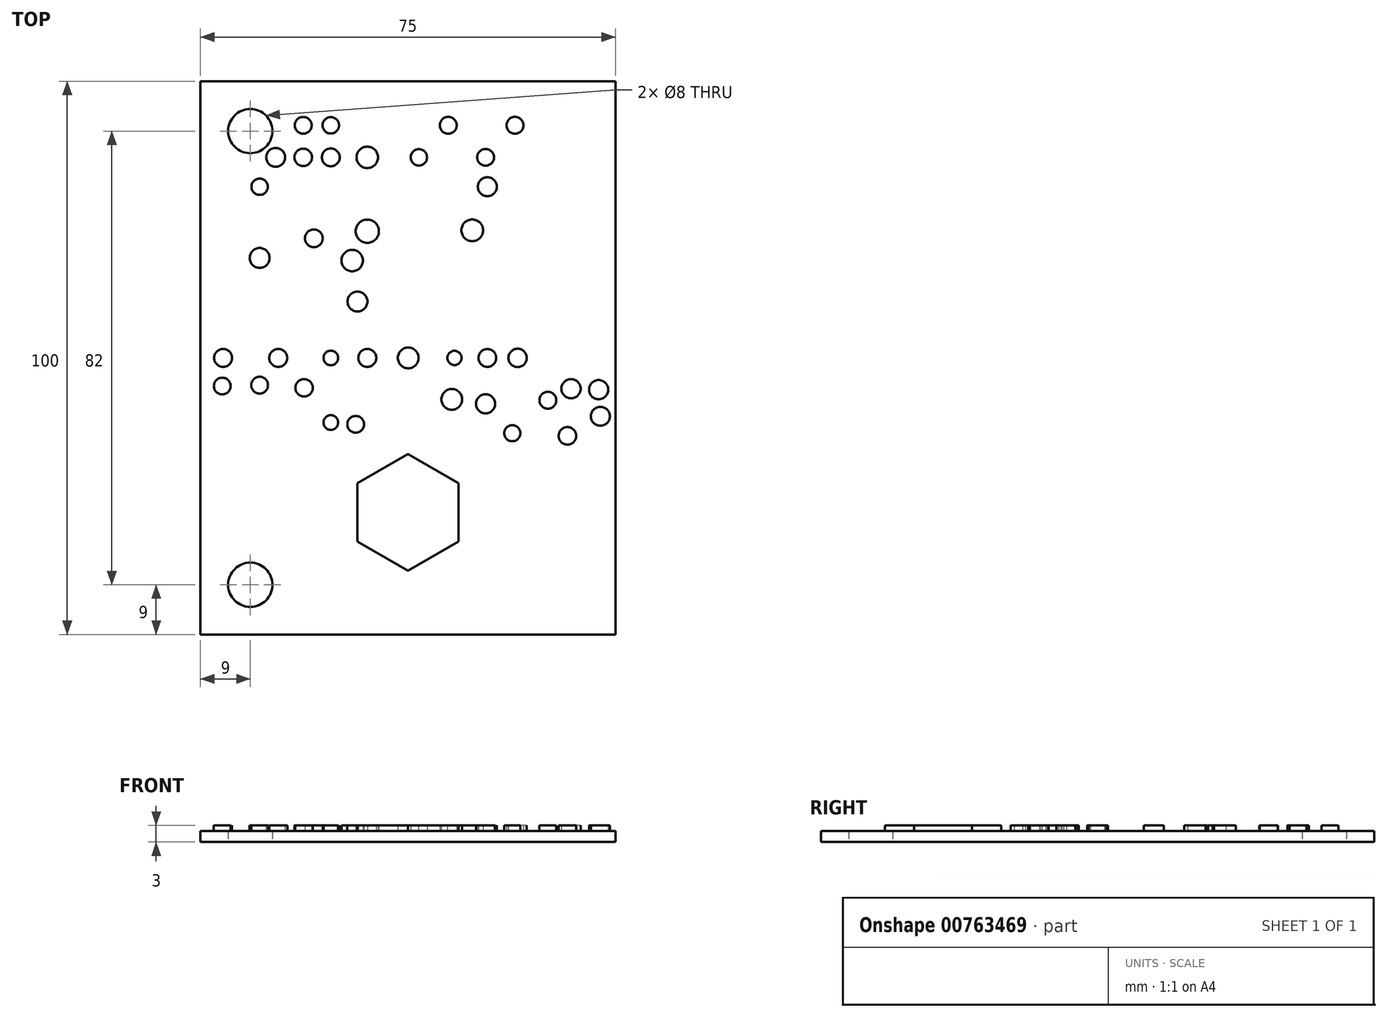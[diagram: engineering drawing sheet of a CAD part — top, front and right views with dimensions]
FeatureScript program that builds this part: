
annotation { "Feature Type Name" : "Feature", "Feature Type Description" : "" }
export const myFeature = defineFeature(function(context is Context, id is Id, definition is map)
    precondition{}
    {
        {
            var Q0;
            Q0=qCreatedBy(makeId("Top.planeOp"),FACE);
            var sketch = newSketch(context, id + "F0", { "sketchPlane" : qUnion([Q0])});
            skLineSegment(sketch, "E0.bottom", {"start": v(-37.5, 50) * mm, "end": v(37.5, 50) * mm});
            skLineSegment(sketch, "E0.top", {"start": v(-37.5, -50) * mm, "end": v(37.5, -50) * mm});
            skLineSegment(sketch, "E0.left", {"start": v(-37.5, 50) * mm, "end": v(-37.5, -50) * mm});
            skLineSegment(sketch, "E0.right", {"start": v(37.5, 50) * mm, "end": v(37.5, -50) * mm});
            skPoint(sketch, "E0.middle", {"position": v(0, 0) * mm});
            skCircle(sketch, "E1", {"center": v(-28.5, 41) * mm, "radius": 4 * mm});
            skCircle(sketch, "E2", {"center": v(-28.5, -41) * mm, "radius": 4 * mm});
            skSolve(sketch);
        }
        {
            var Q0;
            Q0 = qSketchRegion(id + "F0", true);
            var Q1;
            Q1=makeQuery(id+"F0.imprint","IMPRINT",FACE,{"disambiguationData":[TD([[makeQuery(id+"F0.imprint","IMPRINT",EDGE,{"derivedFrom":sQuery(id+"F0.wireOp",EDGE,"E0.bottom")}),-1.0]])]});
            extrude(context, id + "F1", {"entities" : qUnion([Q0, Q1]), "depth" : 2 * mm, "offsetDistance" : 25 * mm});
        }
        {
            var Q0;
            Q0=makeQuery(id+"F1.opExtrude","CAP_FACE",FACE,{"disambiguationData":[OSD([sQuery(id+"F0.wireOp",EDGE,"E0.bottom"),sQuery(id+"F0.wireOp",EDGE,"E0.top"),sQuery(id+"F0.wireOp",EDGE,"E0.left"),sQuery(id+"F0.wireOp",EDGE,"E0.right"),sQuery(id+"F0.wireOp",EDGE,"E1"),sQuery(id+"F0.wireOp",EDGE,"E2")])],"isStart":false});
            var sketch = newSketch(context, id + "F2", { "sketchPlane" : qUnion([Q0])});
            skCircle(sketch, "E3", {"center": v(-18.93, 42.04) * mm, "radius": 1.52 * mm});
            skCircle(sketch, "E4", {"center": v(-18.93, 36.25) * mm, "radius": 1.58 * mm});
            skCircle(sketch, "E5", {"center": v(-23.92, 36.25) * mm, "radius": 1.7 * mm});
            skCircle(sketch, "E6", {"center": v(-26.81, 30.95) * mm, "radius": 1.48 * mm});
            skCircle(sketch, "E7", {"center": v(-13.95, 36.25) * mm, "radius": 1.6 * mm});
            skCircle(sketch, "E8", {"center": v(-7.35, 36.25) * mm, "radius": 1.94 * mm});
            skCircle(sketch, "E9", {"center": v(-13.95, 42.04) * mm, "radius": 1.48 * mm});
            skCircle(sketch, "E10", {"center": v(1.98, 36.25) * mm, "radius": 1.48 * mm});
            skCircle(sketch, "E11", {"center": v(7.28, 42.04) * mm, "radius": 1.53 * mm});
            skCircle(sketch, "E12", {"center": v(14.36, 30.95) * mm, "radius": 1.7 * mm});
            skCircle(sketch, "E13", {"center": v(14.04, 36.25) * mm, "radius": 1.52 * mm});
            skCircle(sketch, "E14", {"center": v(19.35, 42.04) * mm, "radius": 1.53 * mm});
            skCircle(sketch, "E15", {"center": v(-26.81, 18.08) * mm, "radius": 1.8 * mm});
            skCircle(sketch, "E16", {"center": v(-17, 21.62) * mm, "radius": 1.6 * mm});
            skCircle(sketch, "E17", {"center": v(-9.12, 10.2) * mm, "radius": 1.8 * mm});
            skCircle(sketch, "E18", {"center": v(-10.09, 17.6) * mm, "radius": 1.94 * mm});
            skCircle(sketch, "E19", {"center": v(-7.35, 22.9) * mm, "radius": 2.1 * mm});
            skCircle(sketch, "E20", {"center": v(11.63, 23.07) * mm, "radius": 1.96 * mm});
            skCircle(sketch, "E21", {"center": v(-33.4, 0) * mm, "radius": 1.63 * mm});
            skCircle(sketch, "E22", {"center": v(-33.57, -5.08) * mm, "radius": 1.52 * mm});
            skCircle(sketch, "E23", {"center": v(-26.81, -4.92) * mm, "radius": 1.52 * mm});
            skCircle(sketch, "E24", {"center": v(-18.77, -5.4) * mm, "radius": 1.58 * mm});
            skCircle(sketch, "E25", {"center": v(-23.44, 0) * mm, "radius": 1.63 * mm});
            skCircle(sketch, "E26", {"center": v(-13.95, -11.68) * mm, "radius": 1.33 * mm});
            skCircle(sketch, "E27", {"center": v(-9.44, -12) * mm, "radius": 1.52 * mm});
            skCircle(sketch, "E28", {"center": v(-13.95, 0) * mm, "radius": 1.32 * mm});
            skCircle(sketch, "E29", {"center": v(-7.35, 0) * mm, "radius": 1.62 * mm});
            skCircle(sketch, "E30", {"center": v(0.05, 0) * mm, "radius": 1.87 * mm});
            skCircle(sketch, "E31", {"center": v(7.93, -7.5) * mm, "radius": 1.88 * mm});
            skCircle(sketch, "E32", {"center": v(14.04, -8.3) * mm, "radius": 1.73 * mm});
            skCircle(sketch, "E33", {"center": v(8.41, 0) * mm, "radius": 1.3 * mm});
            skCircle(sketch, "E34", {"center": v(14.36, 0) * mm, "radius": 1.6 * mm});
            skCircle(sketch, "E35", {"center": v(18.86, -13.6) * mm, "radius": 1.46 * mm});
            skCircle(sketch, "E36", {"center": v(25.3, -7.65) * mm, "radius": 1.53 * mm});
            skCircle(sketch, "E37", {"center": v(19.83, 0) * mm, "radius": 1.66 * mm});
            skCircle(sketch, "E38", {"center": v(28.84, -14.09) * mm, "radius": 1.58 * mm});
            skCircle(sketch, "E39", {"center": v(34.79, -10.55) * mm, "radius": 1.7 * mm});
            skCircle(sketch, "E40", {"center": v(34.47, -5.72) * mm, "radius": 1.73 * mm});
            skCircle(sketch, "E41", {"center": v(29.48, -5.56) * mm, "radius": 1.74 * mm});
            skCircle(sketch, "E42.cCircle", {"center": v(0, -27.92) * mm, "radius": 9.12 * mm, "construction": true});
            skLineSegment(sketch, "E42.0", {"start": v(-9.12, -33.19) * mm, "end": v(-9.12, -22.65) * mm});
            skLineSegment(sketch, "E42.1", {"start": v(-9.12, -22.65) * mm, "end": v(0, -17.39) * mm});
            skLineSegment(sketch, "E42.2", {"start": v(0, -17.39) * mm, "end": v(9.12, -22.65) * mm});
            skLineSegment(sketch, "E42.3", {"start": v(9.12, -22.65) * mm, "end": v(9.12, -33.19) * mm});
            skLineSegment(sketch, "E42.4", {"start": v(9.12, -33.19) * mm, "end": v(0, -38.45) * mm});
            skLineSegment(sketch, "E42.5", {"start": v(0, -38.45) * mm, "end": v(-9.12, -33.19) * mm});
            skPoint(sketch, "E42.0.midPoint", {"position": v(-9.12, -27.92) * mm});
            skSolve(sketch);
        }
        {
            var Q0;
            Q0=makeQuery(id+"F2.imprint","IMPRINT",FACE,{"disambiguationData":[TD([[makeQuery(id+"F2.imprint","IMPRINT",EDGE,{"derivedFrom":sQuery(id+"F2.wireOp",EDGE,"E42.0")}),-1.0]])]});
            var Q1;
            Q1=makeQuery(id+"F2.imprint","IMPRINT",FACE,{"disambiguationData":[TD([[makeQuery(id+"F2.imprint","IMPRINT",EDGE,{"derivedFrom":sQuery(id+"F2.wireOp",EDGE,"E38")}),1.0]])]});
            var Q2;
            Q2=makeQuery(id+"F2.imprint","IMPRINT",FACE,{"disambiguationData":[TD([[makeQuery(id+"F2.imprint","IMPRINT",EDGE,{"derivedFrom":sQuery(id+"F2.wireOp",EDGE,"E39")}),1.0]])]});
            var Q3;
            Q3=makeQuery(id+"F2.imprint","IMPRINT",FACE,{"disambiguationData":[TD([[makeQuery(id+"F2.imprint","IMPRINT",EDGE,{"derivedFrom":sQuery(id+"F2.wireOp",EDGE,"E40")}),1.0]])]});
            var Q4;
            Q4=makeQuery(id+"F2.imprint","IMPRINT",FACE,{"disambiguationData":[TD([[makeQuery(id+"F2.imprint","IMPRINT",EDGE,{"derivedFrom":sQuery(id+"F2.wireOp",EDGE,"E41")}),1.0]])]});
            var Q5;
            Q5=makeQuery(id+"F2.imprint","IMPRINT",FACE,{"disambiguationData":[TD([[makeQuery(id+"F2.imprint","IMPRINT",EDGE,{"derivedFrom":sQuery(id+"F2.wireOp",EDGE,"E36")}),1.0]])]});
            var Q6;
            Q6=makeQuery(id+"F2.imprint","IMPRINT",FACE,{"disambiguationData":[TD([[makeQuery(id+"F2.imprint","IMPRINT",EDGE,{"derivedFrom":sQuery(id+"F2.wireOp",EDGE,"E35")}),1.0]])]});
            var Q7;
            Q7=makeQuery(id+"F2.imprint","IMPRINT",FACE,{"disambiguationData":[TD([[makeQuery(id+"F2.imprint","IMPRINT",EDGE,{"derivedFrom":sQuery(id+"F2.wireOp",EDGE,"E32")}),1.0]])]});
            var Q8;
            Q8=makeQuery(id+"F2.imprint","IMPRINT",FACE,{"disambiguationData":[TD([[makeQuery(id+"F2.imprint","IMPRINT",EDGE,{"derivedFrom":sQuery(id+"F2.wireOp",EDGE,"E37")}),1.0]])]});
            var Q9;
            Q9=makeQuery(id+"F2.imprint","IMPRINT",FACE,{"disambiguationData":[TD([[makeQuery(id+"F2.imprint","IMPRINT",EDGE,{"derivedFrom":sQuery(id+"F2.wireOp",EDGE,"E34")}),1.0]])]});
            var Q10;
            Q10=makeQuery(id+"F2.imprint","IMPRINT",FACE,{"disambiguationData":[TD([[makeQuery(id+"F2.imprint","IMPRINT",EDGE,{"derivedFrom":sQuery(id+"F2.wireOp",EDGE,"E33")}),1.0]])]});
            var Q11;
            Q11=makeQuery(id+"F2.imprint","IMPRINT",FACE,{"disambiguationData":[TD([[makeQuery(id+"F2.imprint","IMPRINT",EDGE,{"derivedFrom":sQuery(id+"F2.wireOp",EDGE,"E31")}),1.0]])]});
            var Q12;
            Q12=makeQuery(id+"F2.imprint","IMPRINT",FACE,{"disambiguationData":[TD([[makeQuery(id+"F2.imprint","IMPRINT",EDGE,{"derivedFrom":sQuery(id+"F2.wireOp",EDGE,"E27")}),1.0]])]});
            var Q13;
            Q13=makeQuery(id+"F2.imprint","IMPRINT",FACE,{"disambiguationData":[TD([[makeQuery(id+"F2.imprint","IMPRINT",EDGE,{"derivedFrom":sQuery(id+"F2.wireOp",EDGE,"E30")}),1.0]])]});
            var Q14;
            Q14=makeQuery(id+"F2.imprint","IMPRINT",FACE,{"disambiguationData":[TD([[makeQuery(id+"F2.imprint","IMPRINT",EDGE,{"derivedFrom":sQuery(id+"F2.wireOp",EDGE,"E29")}),1.0]])]});
            var Q15;
            Q15=makeQuery(id+"F2.imprint","IMPRINT",FACE,{"disambiguationData":[TD([[makeQuery(id+"F2.imprint","IMPRINT",EDGE,{"derivedFrom":sQuery(id+"F2.wireOp",EDGE,"E28")}),1.0]])]});
            var Q16;
            Q16=makeQuery(id+"F2.imprint","IMPRINT",FACE,{"disambiguationData":[TD([[makeQuery(id+"F2.imprint","IMPRINT",EDGE,{"derivedFrom":sQuery(id+"F2.wireOp",EDGE,"E24")}),1.0]])]});
            var Q17;
            Q17=makeQuery(id+"F2.imprint","IMPRINT",FACE,{"disambiguationData":[TD([[makeQuery(id+"F2.imprint","IMPRINT",EDGE,{"derivedFrom":sQuery(id+"F2.wireOp",EDGE,"E23")}),1.0]])]});
            var Q18;
            Q18=makeQuery(id+"F2.imprint","IMPRINT",FACE,{"disambiguationData":[TD([[makeQuery(id+"F2.imprint","IMPRINT",EDGE,{"derivedFrom":sQuery(id+"F2.wireOp",EDGE,"E26")}),1.0]])]});
            var Q19;
            Q19=makeQuery(id+"F2.imprint","IMPRINT",FACE,{"disambiguationData":[TD([[makeQuery(id+"F2.imprint","IMPRINT",EDGE,{"derivedFrom":sQuery(id+"F2.wireOp",EDGE,"E25")}),1.0]])]});
            var Q20;
            Q20=makeQuery(id+"F2.imprint","IMPRINT",FACE,{"disambiguationData":[TD([[makeQuery(id+"F2.imprint","IMPRINT",EDGE,{"derivedFrom":sQuery(id+"F2.wireOp",EDGE,"E21")}),1.0]])]});
            var Q21;
            Q21=makeQuery(id+"F2.imprint","IMPRINT",FACE,{"disambiguationData":[TD([[makeQuery(id+"F2.imprint","IMPRINT",EDGE,{"derivedFrom":sQuery(id+"F2.wireOp",EDGE,"E22")}),1.0]])]});
            var Q22;
            Q22=makeQuery(id+"F2.imprint","IMPRINT",FACE,{"disambiguationData":[TD([[makeQuery(id+"F2.imprint","IMPRINT",EDGE,{"derivedFrom":sQuery(id+"F2.wireOp",EDGE,"E17")}),1.0]])]});
            var Q23;
            Q23=makeQuery(id+"F2.imprint","IMPRINT",FACE,{"disambiguationData":[TD([[makeQuery(id+"F2.imprint","IMPRINT",EDGE,{"derivedFrom":sQuery(id+"F2.wireOp",EDGE,"E18")}),1.0]])]});
            var Q24;
            Q24=makeQuery(id+"F2.imprint","IMPRINT",FACE,{"disambiguationData":[TD([[makeQuery(id+"F2.imprint","IMPRINT",EDGE,{"derivedFrom":sQuery(id+"F2.wireOp",EDGE,"E19")}),1.0]])]});
            var Q25;
            Q25=makeQuery(id+"F2.imprint","IMPRINT",FACE,{"disambiguationData":[TD([[makeQuery(id+"F2.imprint","IMPRINT",EDGE,{"derivedFrom":sQuery(id+"F2.wireOp",EDGE,"E20")}),1.0]])]});
            var Q26;
            Q26=makeQuery(id+"F2.imprint","IMPRINT",FACE,{"disambiguationData":[TD([[makeQuery(id+"F2.imprint","IMPRINT",EDGE,{"derivedFrom":sQuery(id+"F2.wireOp",EDGE,"E12")}),1.0]])]});
            var Q27;
            Q27=makeQuery(id+"F2.imprint","IMPRINT",FACE,{"disambiguationData":[TD([[makeQuery(id+"F2.imprint","IMPRINT",EDGE,{"derivedFrom":sQuery(id+"F2.wireOp",EDGE,"E13")}),1.0]])]});
            var Q28;
            Q28=makeQuery(id+"F2.imprint","IMPRINT",FACE,{"disambiguationData":[TD([[makeQuery(id+"F2.imprint","IMPRINT",EDGE,{"derivedFrom":sQuery(id+"F2.wireOp",EDGE,"E14")}),1.0]])]});
            var Q29;
            Q29=makeQuery(id+"F2.imprint","IMPRINT",FACE,{"disambiguationData":[TD([[makeQuery(id+"F2.imprint","IMPRINT",EDGE,{"derivedFrom":sQuery(id+"F2.wireOp",EDGE,"E11")}),1.0]])]});
            var Q30;
            Q30=makeQuery(id+"F2.imprint","IMPRINT",FACE,{"disambiguationData":[TD([[makeQuery(id+"F2.imprint","IMPRINT",EDGE,{"derivedFrom":sQuery(id+"F2.wireOp",EDGE,"E10")}),1.0]])]});
            var Q31;
            Q31=makeQuery(id+"F2.imprint","IMPRINT",FACE,{"disambiguationData":[TD([[makeQuery(id+"F2.imprint","IMPRINT",EDGE,{"derivedFrom":sQuery(id+"F2.wireOp",EDGE,"E8")}),1.0]])]});
            var Q32;
            Q32=makeQuery(id+"F2.imprint","IMPRINT",FACE,{"disambiguationData":[TD([[makeQuery(id+"F2.imprint","IMPRINT",EDGE,{"derivedFrom":sQuery(id+"F2.wireOp",EDGE,"E7")}),1.0]])]});
            var Q33;
            Q33=makeQuery(id+"F2.imprint","IMPRINT",FACE,{"disambiguationData":[TD([[makeQuery(id+"F2.imprint","IMPRINT",EDGE,{"derivedFrom":sQuery(id+"F2.wireOp",EDGE,"E9")}),1.0]])]});
            var Q34;
            Q34=makeQuery(id+"F2.imprint","IMPRINT",FACE,{"disambiguationData":[TD([[makeQuery(id+"F2.imprint","IMPRINT",EDGE,{"derivedFrom":sQuery(id+"F2.wireOp",EDGE,"E3")}),1.0]])]});
            var Q35;
            Q35=makeQuery(id+"F2.imprint","IMPRINT",FACE,{"disambiguationData":[TD([[makeQuery(id+"F2.imprint","IMPRINT",EDGE,{"derivedFrom":sQuery(id+"F2.wireOp",EDGE,"E4")}),1.0]])]});
            var Q36;
            Q36=makeQuery(id+"F2.imprint","IMPRINT",FACE,{"disambiguationData":[TD([[makeQuery(id+"F2.imprint","IMPRINT",EDGE,{"derivedFrom":sQuery(id+"F2.wireOp",EDGE,"E5")}),1.0]])]});
            var Q37;
            Q37=makeQuery(id+"F2.imprint","IMPRINT",FACE,{"disambiguationData":[TD([[makeQuery(id+"F2.imprint","IMPRINT",EDGE,{"derivedFrom":sQuery(id+"F2.wireOp",EDGE,"E6")}),1.0]])]});
            var Q38;
            Q38=makeQuery(id+"F2.imprint","IMPRINT",FACE,{"disambiguationData":[TD([[makeQuery(id+"F2.imprint","IMPRINT",EDGE,{"derivedFrom":sQuery(id+"F2.wireOp",EDGE,"E15")}),1.0]])]});
            var Q39;
            Q39=makeQuery(id+"F2.imprint","IMPRINT",FACE,{"disambiguationData":[TD([[makeQuery(id+"F2.imprint","IMPRINT",EDGE,{"derivedFrom":sQuery(id+"F2.wireOp",EDGE,"E16")}),1.0]])]});
            extrude(context, id + "F3", {"entities" : qUnion([Q0, Q1, Q2, Q3, Q4, Q5, Q6, Q7, Q8, Q9, Q10, Q11, Q12, Q13, Q14, Q15, Q16, Q17, Q18, Q19, Q20, Q21, Q22, Q23, Q24, Q25, Q26, Q27, Q28, Q29, Q30, Q31, Q32, Q33, Q34, Q35, Q36, Q37, Q38, Q39]), "operationType" : NewBodyOperationType.ADD, "depth" : 1 * mm, "offsetDistance" : 25 * mm});
        }
    });
